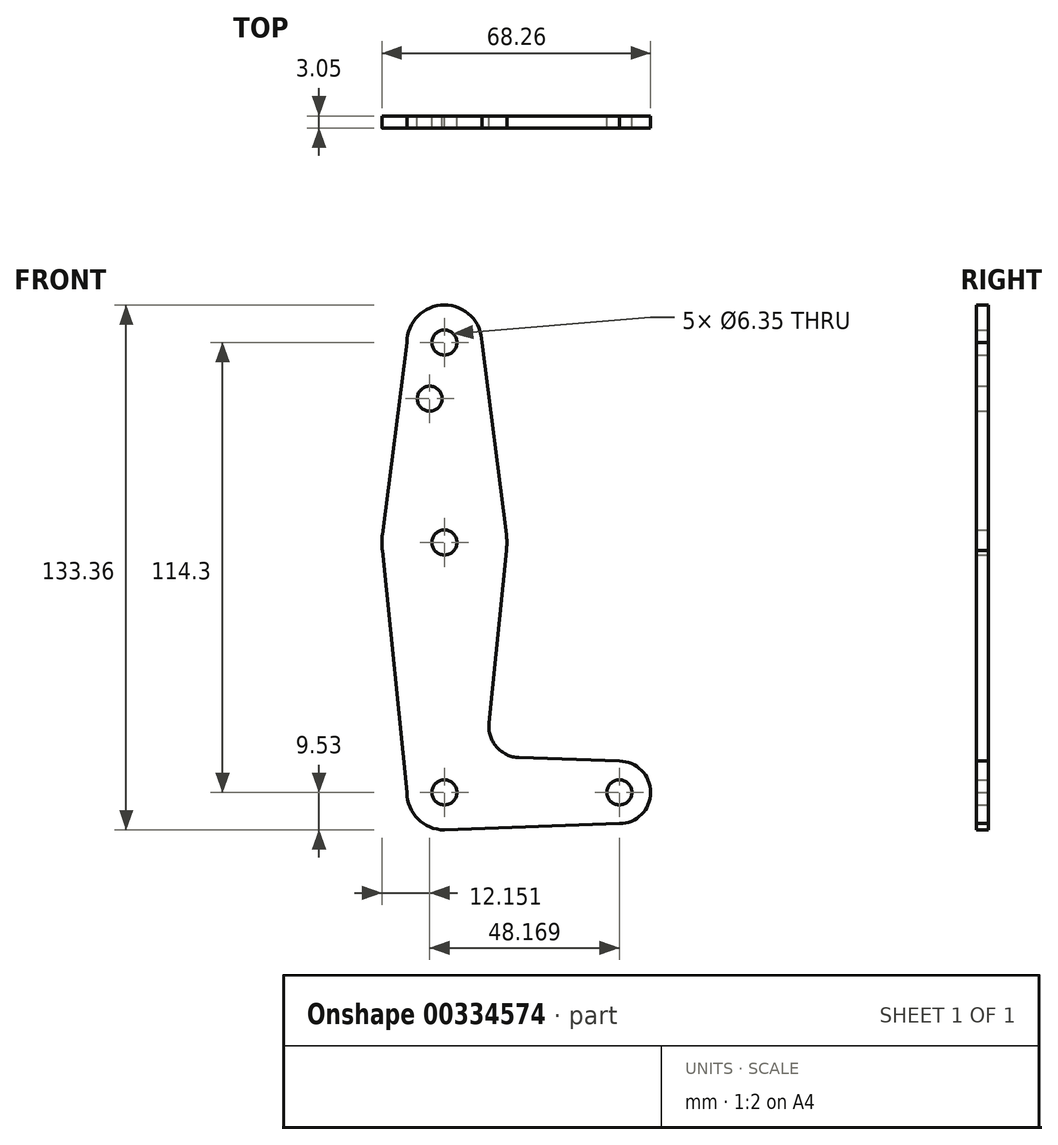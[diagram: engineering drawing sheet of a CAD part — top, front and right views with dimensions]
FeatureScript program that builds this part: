
annotation { "Feature Type Name" : "Feature", "Feature Type Description" : "" }
export const myFeature = defineFeature(function(context is Context, id is Id, definition is map)
    precondition{}
    {
        {
            var Q0;
            Q0=qCreatedBy(makeId("Front.planeOp"),FACE);
            var sketch = newSketch(context, id + "F0", { "sketchPlane" : qUnion([Q0])});
            skLineSegment(sketch, "E0", {"start": v(0, 0) * mm, "end": v(0, 114.3) * mm, "construction": true});
            skLineSegment(sketch, "E1", {"start": v(0, 0) * mm, "end": v(44.45, 0) * mm, "construction": true});
            skCircle(sketch, "E2", {"center": v(0, 0) * mm, "radius": 9.53 * mm});
            skCircle(sketch, "E3", {"center": v(44.45, 0) * mm, "radius": 7.94 * mm});
            skCircle(sketch, "E4", {"center": v(0, 114.3) * mm, "radius": 9.53 * mm});
            skCircle(sketch, "E5", {"center": v(0, 63.5) * mm, "radius": 15.88 * mm});
            skLineSegment(sketch, "E6", {"start": v(9.52, 114.3) * mm, "end": v(15.75, 65.5) * mm});
            skLineSegment(sketch, "E7", {"start": v(-9.53, 114.3) * mm, "end": v(-15.75, 65.5) * mm});
            skLineSegment(sketch, "E8", {"start": v(15.75, 61.5) * mm, "end": v(11.34, 17.59) * mm});
            skLineSegment(sketch, "E9", {"start": v(-15.75, 61.5) * mm, "end": v(-9.53, 0) * mm});
            skLineSegment(sketch, "E10", {"start": v(0, -9.52) * mm, "end": v(44.45, -7.94) * mm});
            skLineSegment(sketch, "E11", {"start": v(18.97, 8.85) * mm, "end": v(44.45, 7.94) * mm});
            skCircle(sketch, "E12", {"center": v(0, 114.3) * mm, "radius": 3.18 * mm});
            skCircle(sketch, "E13", {"center": v(0, 63.5) * mm, "radius": 3.18 * mm});
            skCircle(sketch, "E14", {"center": v(0, 0) * mm, "radius": 3.18 * mm});
            skCircle(sketch, "E15", {"center": v(44.45, 0) * mm, "radius": 3.18 * mm});
            skCircle(sketch, "E16", {"center": v(-3.72, 100.03) * mm, "radius": 3.18 * mm});
            skArc(sketch, "E17.filletArc", {"start": v(11.34, 17.59) * mm, "mid": v(13.26, 11.57) * mm, "end": v(18.97, 8.85) * mm});
            skSolve(sketch);
        }
        {
            var Q0;
            {var subQ1=sQuery(id+"F0.wireOp",EDGE,"E6");Q0=makeQuery(id+"F0.imprint","IMPRINT",FACE,{"disambiguationData":[TD([[makeQuery(id+"F0.imprint","IMPRINT",EDGE,{"derivedFrom":subQ1}),-1.0]])]});}
            var Q1;
            Q1=makeQuery(id+"F0.imprint","IMPRINT",FACE,{"disambiguationData":[TD([[makeQuery(id+"F0.imprint","IMPRINT",EDGE,{"derivedFrom":sQuery(id+"F0.wireOp",EDGE,"E12")}),-1.0]])]});
            var Q2;
            Q2=makeQuery(id+"F0.imprint","IMPRINT",FACE,{"disambiguationData":[TD([[makeQuery(id+"F0.imprint","IMPRINT",EDGE,{"derivedFrom":sQuery(id+"F0.wireOp",EDGE,"E13")}),-1.0]])]});
            var Q3;
            {var subQ0=sQuery(id+"F0.wireOp",EDGE,"E8");Q3=makeQuery(id+"F0.imprint","IMPRINT",FACE,{"disambiguationData":[TD([[makeQuery(id+"F0.imprint","IMPRINT",EDGE,{"derivedFrom":subQ0}),-1.0]])]});}
            var Q4;
            Q4=makeQuery(id+"F0.imprint","IMPRINT",FACE,{"disambiguationData":[TD([[makeQuery(id+"F0.imprint","IMPRINT",EDGE,{"derivedFrom":sQuery(id+"F0.wireOp",EDGE,"E14")}),-1.0]])]});
            var Q5;
            Q5=makeQuery(id+"F0.imprint","IMPRINT",FACE,{"disambiguationData":[TD([[makeQuery(id+"F0.imprint","IMPRINT",EDGE,{"derivedFrom":sQuery(id+"F0.wireOp",EDGE,"E15")}),-1.0]])]});
            extrude(context, id + "F1", {"entities" : qUnion([Q0, Q1, Q2, Q3, Q4, Q5]), "depth" : 3.05 * mm});
        }
    });
